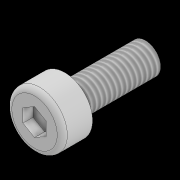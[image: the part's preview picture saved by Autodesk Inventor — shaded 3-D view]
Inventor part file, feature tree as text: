
AUTODESK INVENTOR PART (.ipt)
format: ipt  version: 2022.2 (Build 262287010, 287A)  size: 119,296 bytes
history: native  units: mm
features: extrude x3, sketch x1, fillet x1, thread x1
ambient origin geometry x8: Origin, YZ Plane, XZ Plane, XY Plane, X Axis, Y Axis, Z Axis, Center Point
bodies: Body1 (feature_tree)
feature tree (6):
  sketch  "Sketch3"  dims[d8=1.5mm d9=2.75mm d10=2.3mm d11=3.0mm d12=0.0mm d13=8.0mm d14=0.0mm d15=1.0mm d16=0.0mm d17=0.5mm d18=8.0mm d19=0.0mm]
  extrude  "Extrusion1"  Depth=2.75mm
  extrude  "Extrusion2"  Depth=2.3mm
  extrude  "Extrusion3"  Depth=3.0mm
  fillet  "Fillet1"  [1 undecoded]
  thread  "Thread2"  [1 undecoded]
note: 2 required parameter values undecoded (feature->parameter linkage not recoverable at this tier; creation-order binding heuristic only, values carry confidence <= 0.55)
